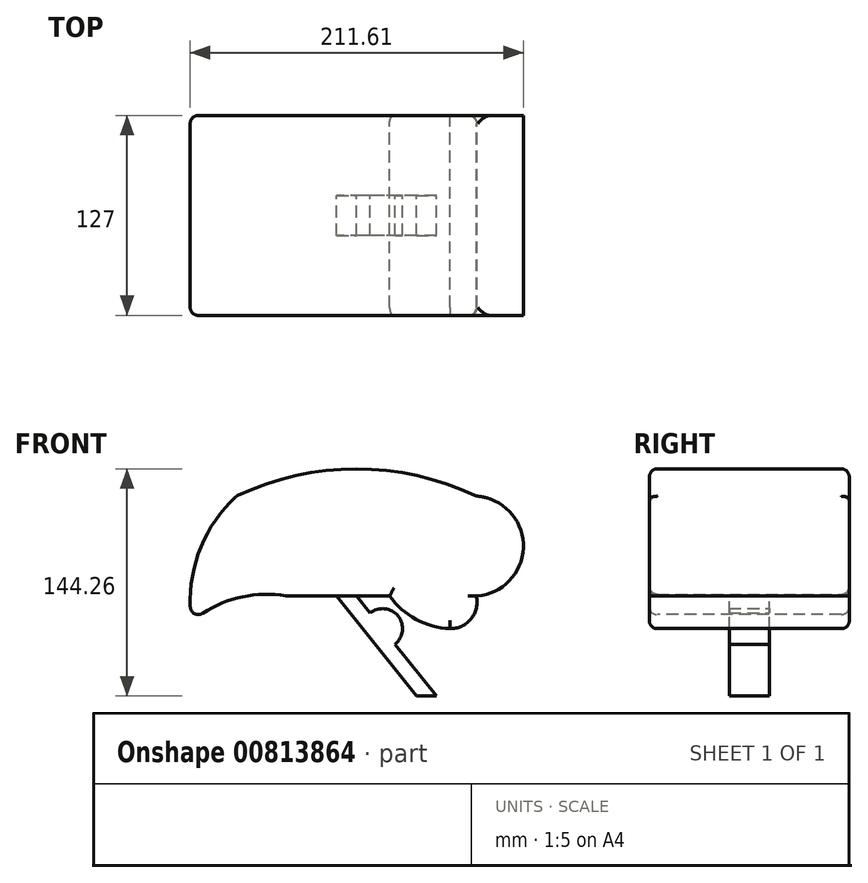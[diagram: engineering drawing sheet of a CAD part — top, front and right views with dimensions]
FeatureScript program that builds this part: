
annotation { "Feature Type Name" : "Feature", "Feature Type Description" : "" }
export const myFeature = defineFeature(function(context is Context, id is Id, definition is map)
    precondition{}
    {
        {
            var Q0;
            Q0=qCreatedBy(makeId("Front.planeOp"),FACE);
            var sketch = newSketch(context, id + "F0", { "sketchPlane" : qUnion([Q0])});
            skLineSegment(sketch, "E0", {"start": v(-43.93, 20.69) * mm, "end": v(-31.23, 20.69) * mm});
            skLineSegment(sketch, "E1", {"start": v(-43.93, 20.69) * mm, "end": v(-75.68, 20.69) * mm});
            skLineSegment(sketch, "E2", {"start": v(-31.23, 20.69) * mm, "end": v(-10.17, 20.69) * mm});
            skLineSegment(sketch, "E3", {"start": v(19.57, -42.81) * mm, "end": v(-6.75, -9.92) * mm});
            skLineSegment(sketch, "E4", {"start": v(6.87, -42.81) * mm, "end": v(-43.93, 20.69) * mm});
            skPoint(sketch, "E5.start.orphan", {"position": v(-43.93, -42.81) * mm});
            skPoint(sketch, "E6.start.orphan", {"position": v(-31.23, -42.81) * mm});
            skLineSegment(sketch, "E7", {"start": v(6.87, -42.81) * mm, "end": v(19.57, -42.81) * mm});
            skArc(sketch, "E8", {"start": v(-6.75, -9.92) * mm, "mid": v(-4.76, 7.93) * mm, "end": v(-22.61, 9.92) * mm});
            skLineSegment(sketch, "E9.trimOffspring", {"start": v(-22.61, 9.92) * mm, "end": v(-31.23, 20.69) * mm});
            skPoint(sketch, "E10.end.orphan", {"position": v(-107.43, 20.69) * mm});
            skArc(sketch, "E11", {"start": v(44.97, 20.69) * mm, "mid": v(74.76, 52.44) * mm, "end": v(44.97, 84.19) * mm});
            skArc(sketch, "E12", {"start": v(44.97, 84.19) * mm, "mid": v(-31.23, 101.45) * mm, "end": v(-107.43, 84.19) * mm});
            skPoint(sketch, "E13.end.orphan", {"position": v(-107.43, -17.41) * mm});
            skArc(sketch, "E14", {"start": v(-107.43, 84.19) * mm, "mid": v(-131.58, 47.9) * mm, "end": v(-135.91, 4.52) * mm});
            skArc(sketch, "E15", {"start": v(-75.68, 20.69) * mm, "mid": v(-107.6, 19.28) * mm, "end": v(-135.91, 4.52) * mm});
            skArc(sketch, "E16", {"start": v(28.07, 0) * mm, "mid": v(41.59, 6.2) * mm, "end": v(44.97, 20.69) * mm});
            skArc(sketch, "E17", {"start": v(-10.17, 20.69) * mm, "mid": v(6.57, 5.94) * mm, "end": v(28.07, 0) * mm});
            skSolve(sketch);
        }
        {
            var Q0;
            Q0=makeQuery(id+"F0.imprint","IMPRINT",FACE,{"disambiguationData":[TD([[makeQuery(id+"F0.imprint","IMPRINT",EDGE,{"derivedFrom":sQuery(id+"F0.wireOp",EDGE,"E0")}),-1.0]])]});
            extrude(context, id + "F1", {"entities" : qUnion([Q0]), "depth" : 12.7 * mm, "offsetDistance" : 25.4 * mm});
        }
        {
            var Q0;
            Q0=makeQuery(id+"F0.imprint","IMPRINT",FACE,{"disambiguationData":[TD([[makeQuery(id+"F0.imprint","IMPRINT",EDGE,{"derivedFrom":sQuery(id+"F0.wireOp",EDGE,"E0")}),1.0]])]});
            var Q1;
            Q1=makeQuery(id+"F0.imprint","IMPRINT",FACE,{"disambiguationData":[TD([[makeQuery(id+"F0.imprint","IMPRINT",EDGE,{"derivedFrom":sQuery(id+"F0.wireOp",EDGE,"9KRWaGh5-BUAy-Q4HC-506H-MNtPb0ZihwdE")}),1.0]])]});
            extrude(context, id + "F2", {"entities" : qUnion([Q0, Q1]), "operationType" : NewBodyOperationType.ADD, "depth" : 63.5 * mm, "offsetDistance" : 25.4 * mm});
        }
        {
            var Q0;
            Q0=makeQuery(id+"F2.opExtrude","CAP_EDGE",EDGE,{"disambiguationData":[OSD([sQuery(id+"F0.wireOp",EDGE,"E12")])],"isStart":false});
            var Q1;
            Q1=makeQuery(id+"F2.opExtrude","CAP_EDGE",EDGE,{"disambiguationData":[OSD([sQuery(id+"F0.wireOp",EDGE,"E14")])],"isStart":false});
            var Q2;
            Q2=makeQuery(id+"F2.opExtrude","SWEPT_EDGE",EDGE,{"disambiguationData":[OSD([sQuery(id+"F0.wireOp",EDGE,"E12"),sQuery(id+"F0.wireOp",EDGE,"E14")])]});
            var Q3;
            Q3=makeQuery(id+"F2.opExtrude","SWEPT_EDGE",EDGE,{"disambiguationData":[OSD([sQuery(id+"F0.wireOp",EDGE,"E11"),sQuery(id+"F0.wireOp",EDGE,"E12")])]});
            var Q4;
            Q4=makeQuery(id+"F2.opExtrude","CAP_EDGE",EDGE,{"disambiguationData":[OSD([sQuery(id+"F0.wireOp",EDGE,"E15")])],"isStart":false});
            var Q5;
            Q5=makeQuery(id+"F2.opExtrude","CAP_EDGE",EDGE,{"disambiguationData":[OSD([sQuery(id+"F0.wireOp",EDGE,"E0"),sQuery(id+"F0.wireOp",EDGE,"E1"),sQuery(id+"F0.wireOp",EDGE,"E2")])],"isStart":false});
            var Q6;
            Q6=makeQuery(id+"F2.opExtrude","SWEPT_EDGE",EDGE,{"disambiguationData":[OSD([sQuery(id+"F0.wireOp",EDGE,"E1"),sQuery(id+"F0.wireOp",EDGE,"E15")])]});
            var Q7;
            Q7=makeQuery(id+"F2.opExtrude","SWEPT_EDGE",EDGE,{"disambiguationData":[OSD([sQuery(id+"F0.wireOp",EDGE,"E14"),sQuery(id+"F0.wireOp",EDGE,"E15")])]});
            var Q8;
            Q8=makeQuery(id+"F2.opExtrude","CAP_EDGE",EDGE,{"disambiguationData":[OSD([sQuery(id+"F0.wireOp",EDGE,"E17")])],"isStart":false});
            var Q9;
            Q9=makeQuery(id+"F2.opExtrude","CAP_EDGE",EDGE,{"disambiguationData":[OSD([sQuery(id+"F0.wireOp",EDGE,"E16")])],"isStart":false});
            fillet(context, id + "F3", {"entities" : qUnion([Q0, Q1, Q2, Q3, Q4, Q5, Q6, Q7, Q8, Q9]), "radius" : 5.08 * mm, "tangentPropagation" : true, "allowEdgeOverflow" : false});
        }
        {
            var Q0;
            Q0=makeQuery(id+"F0.imprint","IMPRINT",FACE,{"disambiguationData":[TD([[makeQuery(id+"F0.imprint","IMPRINT",EDGE,{"derivedFrom":sQuery(id+"F0.wireOp",EDGE,"E0")}),1.0]])]});
            cPlane(context, id + "F4", {"entities" : qUnion([Q0]), "cplaneType" : CPlaneType.OFFSET, "offset" : 0 * mm, "width" : 152.4 * mm, "height" : 152.4 * mm});
        }
        {
            var Q0;
            Q0=makeQuery(id+"F1.opExtrude","SWEPT_BODY",BODY,{"disambiguationData":[OSD([sQuery(id+"F0.wireOp",EDGE,"E0"),sQuery(id+"F0.wireOp",EDGE,"E3"),sQuery(id+"F0.wireOp",EDGE,"E4"),sQuery(id+"F0.wireOp",EDGE,"E7"),sQuery(id+"F0.wireOp",EDGE,"E8"),sQuery(id+"F0.wireOp",EDGE,"E9.trimOffspring")])]});
            var Q1;
            Q1=qCreatedBy(id+"F4.planeOp",FACE);
            mirror(context, id + "F5", {"operationType" : NewBodyOperationType.ADD, "entities" : qUnion([Q0]), "mirrorPlane" : qUnion([Q1])});
        }
    });
